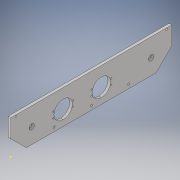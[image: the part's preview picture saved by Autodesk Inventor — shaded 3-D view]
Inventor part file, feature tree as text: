
AUTODESK INVENTOR PART (.ipt)
format: ipt  version: 2017 (Build 210142000, 142)  size: 200,192 bytes
history: native  units: in
note: dims shown in document units (in); Inventor stores cm internally (conversion verified against a paired STEP export)
features: sketch x9, hole x5, extrude x2, chamfer x2, projected_geometry x1
ambient origin geometry x8: Origin, YZ Plane, XZ Plane, XY Plane, X Axis, Y Axis, Z Axis, Center Point
bodies: Solid1 (feature_tree)
feature tree (19):
  extrude  "Extrusion1"  Depth=15.5in
  sketch  "Sketch3"  dims[d4=2.0in]
  sketch  "Sketch4"  dims[d5=1.0in]
  chamfer  "Chamfer1"  Distance=0.25in
  chamfer  "Chamfer2"  Distance=1.5in Angle=45.0deg
  hole  "Hole1"  [1 undecoded]
  hole  "Hole3"  [1 undecoded]
  sketch  "Sketch8"  dims[d13=1.5in d14=0.125in d15=45.0deg d16=2.0in]
  sketch  "Sketch9"  dims[d17=1.5in d18=1.5in]
  hole  "Hole4"  [1 undecoded]
  hole  "Hole5"  [1 undecoded]
  hole  "Hole6"  [1 undecoded]
  extrude  "Extrusion2"  Depth=0.25in
  sketch  "Sketch1"  dims[d2=3.25in d3=15.5in]
  sketch  "Sketch5"  dims[d6=2.0in]
  projected_geometry  "Projected Loop1"
  sketch  "Sketch7"  dims[d7=1.0in d8=0.25in d9=0.0in d10=1.5in d11=0.125in d12=45.0deg]
  sketch  "Sketch10"  dims[d19=2.0in]
  sketch  "Sketch14"  dims[d20=0.501in d21=0.75in d22=0.375in d23=0.25in d24=0.5635in d25=1.0in d26=0.8108in d42=0.394in d43=3.75in d44=3.75in d45=0.144in d46=0.5in d47=0.5in d48=0.188in d49=0.75in d50=0.375in d51=0.25in d52=0.5635in d53=1.0in d54=0.8108in d55=7.75in d56=0.144in d57=0.394in d58=0.394in d59=4.166in d60=4.166in d61=0.188in d62=0.75in d63=0.375in d64=0.25in d65=0.5635in d66=1.0in d67=0.8108in d68=0.188in d69=0.75in d70=0.375in d71=0.25in d72=0.5635in d73=1.0in d74=0.8108in d75=1.7in d76=0.75in d77=0.375in d78=0.25in d79=0.5635in d80=1.0in d81=0.8108in d82=0.144in d108=1.82in d109=1.82in d113=0.945in d114=0.276in d115=0.276in d116=0.945in d117=0.945in d118=0.945in d119=0.138in d120=0.138in d121=0.138in d122=0.138in d123=0.138in d124=1.0in d125=0.0in]
note: 5 required parameter values undecoded (feature->parameter linkage not recoverable at this tier; creation-order binding heuristic only, values carry confidence <= 0.55)
